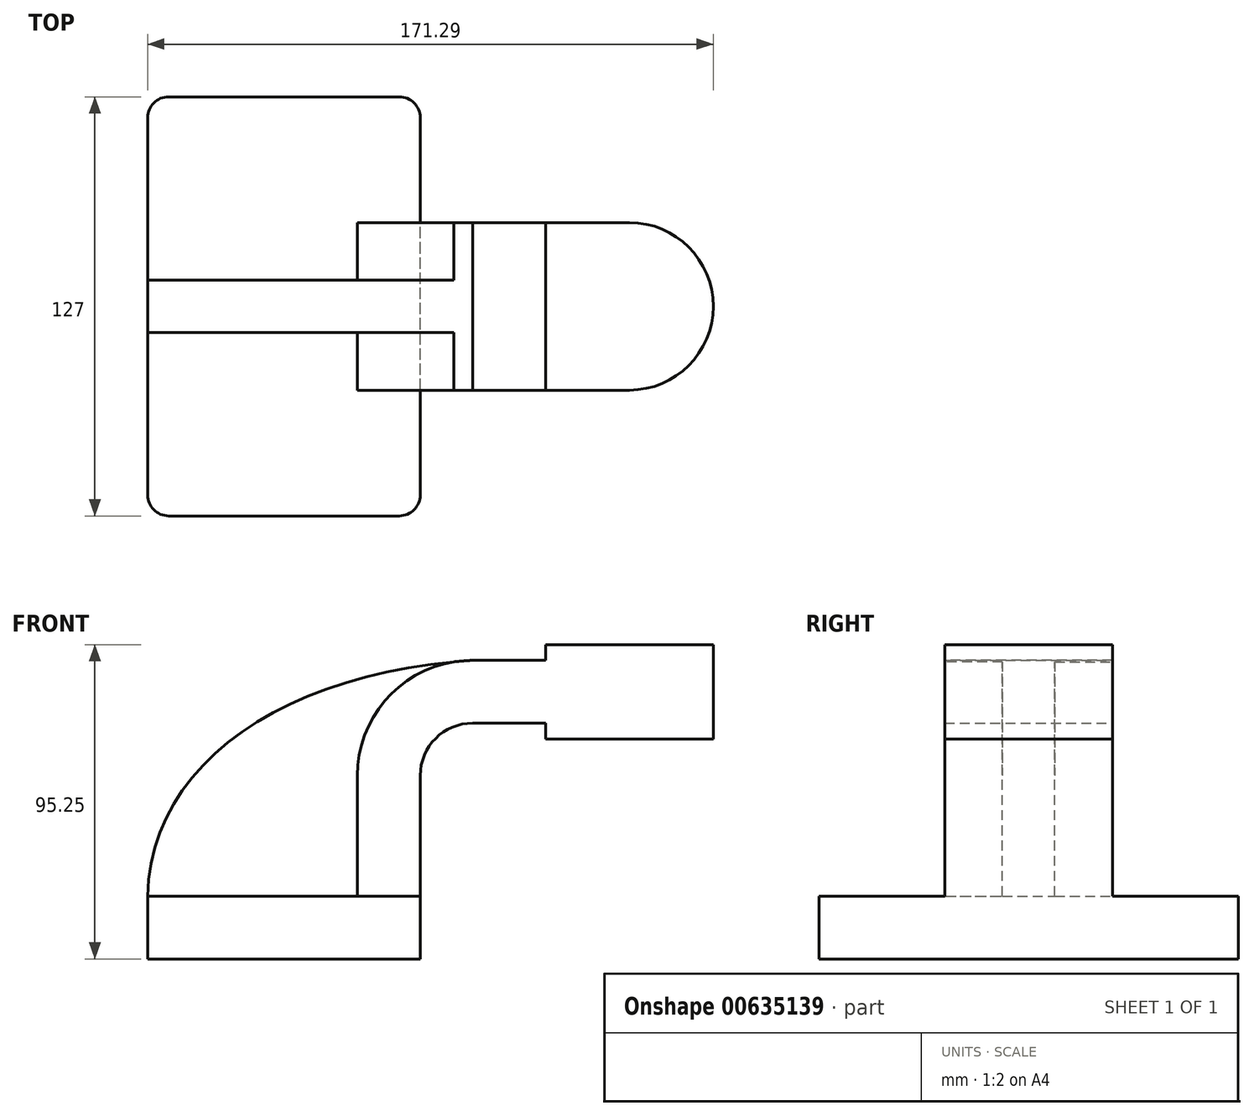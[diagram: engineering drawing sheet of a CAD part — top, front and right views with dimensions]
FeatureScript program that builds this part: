
annotation { "Feature Type Name" : "Feature", "Feature Type Description" : "" }
export const myFeature = defineFeature(function(context is Context, id is Id, definition is map)
    precondition{}
    {
        {
            var Q0;
            Q0=qCreatedBy(makeId("Front.planeOp"),FACE);
            var sketch = newSketch(context, id + "F0", { "sketchPlane" : qUnion([Q0])});
            skLineSegment(sketch, "E0.bottom", {"start": v(-41.28, -9.53) * mm, "end": v(41.28, -9.53) * mm});
            skLineSegment(sketch, "E0.top", {"start": v(-41.28, 9.52) * mm, "end": v(41.28, 9.52) * mm});
            skLineSegment(sketch, "E0.left", {"start": v(-41.28, -9.53) * mm, "end": v(-41.28, 9.52) * mm});
            skLineSegment(sketch, "E0.right", {"start": v(41.28, -9.53) * mm, "end": v(41.28, 9.52) * mm});
            skPoint(sketch, "E0.middle", {"position": v(0, 0) * mm});
            skLineSegment(sketch, "E1.bottom", {"start": v(130.01, 57.15) * mm, "end": v(79.21, 57.15) * mm});
            skLineSegment(sketch, "E1.top", {"start": v(130.01, 85.73) * mm, "end": v(79.21, 85.73) * mm});
            skLineSegment(sketch, "E1.left", {"start": v(130.01, 57.15) * mm, "end": v(130.01, 85.73) * mm});
            skLineSegment(sketch, "E1.right", {"start": v(79.21, 57.15) * mm, "end": v(79.21, 85.73) * mm});
            skPoint(sketch, "E1.middle", {"position": v(104.61, 71.44) * mm});
            skLineSegment(sketch, "E2", {"start": v(41.27, 9.52) * mm, "end": v(41.27, 46.05) * mm});
            skArc(sketch, "E3", {"start": v(41.27, 46.05) * mm, "mid": v(45.92, 57.28) * mm, "end": v(57.15, 61.93) * mm});
            skLineSegment(sketch, "E4", {"start": v(57.15, 61.93) * mm, "end": v(85.72, 61.93) * mm});
            skLineSegment(sketch, "E5.0", {"start": v(57.15, 80.98) * mm, "end": v(85.72, 80.98) * mm});
            skArc(sketch, "E5.1", {"start": v(22.22, 46.05) * mm, "mid": v(32.45, 70.75) * mm, "end": v(57.15, 80.98) * mm});
            skLineSegment(sketch, "E5.2", {"start": v(22.22, 9.52) * mm, "end": v(22.22, 46.05) * mm});
            skLineSegment(sketch, "E6", {"start": v(104.61, 57.15) * mm, "end": v(104.61, 85.73) * mm});
            skFitSpline(sketch, "E7", {"points": [v(-41.28, 9.52) * mm, v(57.15, 80.98) * mm], "startDerivative": vector(2.6, 121.25) * mm, "endDerivative": vector(171.45, 11.58) * mm});
            skSolve(sketch);
        }
        {
            var Q0;
            Q0=makeQuery(id+"F0.imprint","IMPRINT",FACE,{"disambiguationData":[TD([[makeQuery(id+"F0.imprint","IMPRINT",EDGE,{"derivedFrom":sQuery(id+"F0.wireOp",EDGE,"E0.bottom")}),1.0]])]});
            extrude(context, id + "F1", {"entities" : qUnion([Q0]), "endBound" : BoundingType.SYMMETRIC, "depth" : 127 * mm, "offsetDistance" : 25.4 * mm});
        }
        {
            var Q0;
            {var subQ1=sQuery(id+"F0.wireOp",EDGE,"E2");Q0=makeQuery(id+"F0.imprint","IMPRINT",FACE,{"disambiguationData":[TD([[makeQuery(id+"F0.imprint","IMPRINT",EDGE,{"derivedFrom":subQ1}),1.0]])]});}
            var Q1;
            {var subQ6=sQuery(id+"F0.wireOp",EDGE,"E6");Q1=makeQuery(id+"F0.imprint","IMPRINT",FACE,{"disambiguationData":[TD([[makeQuery(id+"F0.imprint","IMPRINT",EDGE,{"derivedFrom":subQ6}),1.0]])]});}
            extrude(context, id + "F2", {"entities" : qUnion([Q0, Q1]), "operationType" : NewBodyOperationType.ADD, "endBound" : BoundingType.SYMMETRIC, "depth" : 50.8 * mm, "offsetDistance" : 25.4 * mm});
        }
        {
            var Q0;
            {var subQ3=sQuery(id+"F0.wireOp",EDGE,"E5.2");Q0=makeQuery(id+"F0.imprint","IMPRINT",FACE,{"disambiguationData":[TD([[makeQuery(id+"F0.imprint","IMPRINT",EDGE,{"derivedFrom":subQ3}),1.0]])]});}
            extrude(context, id + "F3", {"entities" : qUnion([Q0]), "operationType" : NewBodyOperationType.ADD, "endBound" : BoundingType.SYMMETRIC, "depth" : 15.88 * mm, "offsetDistance" : 25.4 * mm});
        }
        {
            var Q0;
            {var subQ0=sQuery(id+"F0.wireOp",EDGE,"E1.left");Q0=makeQuery(id+"F0.imprint","IMPRINT",FACE,{"disambiguationData":[TD([[makeQuery(id+"F0.imprint","IMPRINT",EDGE,{"derivedFrom":subQ0}),1.0]])]});}
            var Q1;
            Q1=sQuery(id+"F0.wireOp",EDGE,"E6");
            revolve(context, id + "F4", {"operationType" : NewBodyOperationType.ADD, "entities" : qUnion([Q0]), "axis" : qUnion([Q1]), "revolveType" : RevolveType.FULL});
        }
        {
            var Q0;
            Q0=makeQuery(id+"F1.opExtrude","CAP_EDGE",EDGE,{"disambiguationData":[OSD([sQuery(id+"F0.wireOp",EDGE,"E0.right")])],"isStart":false});
            var Q1;
            Q1=makeQuery(id+"F1.opExtrude","CAP_EDGE",EDGE,{"disambiguationData":[OSD([sQuery(id+"F0.wireOp",EDGE,"E0.right")])],"isStart":true});
            var Q2;
            Q2=makeQuery(id+"F1.opExtrude","CAP_EDGE",EDGE,{"disambiguationData":[OSD([sQuery(id+"F0.wireOp",EDGE,"E0.left")])],"isStart":true});
            var Q3;
            Q3=makeQuery(id+"F1.opExtrude","CAP_EDGE",EDGE,{"disambiguationData":[OSD([sQuery(id+"F0.wireOp",EDGE,"E0.left")])],"isStart":false});
            fillet(context, id + "F5", {"entities" : qUnion([Q0, Q1, Q2, Q3]), "radius" : 6.35 * mm, "tangentPropagation" : true, "allowEdgeOverflow" : false});
        }
    });
